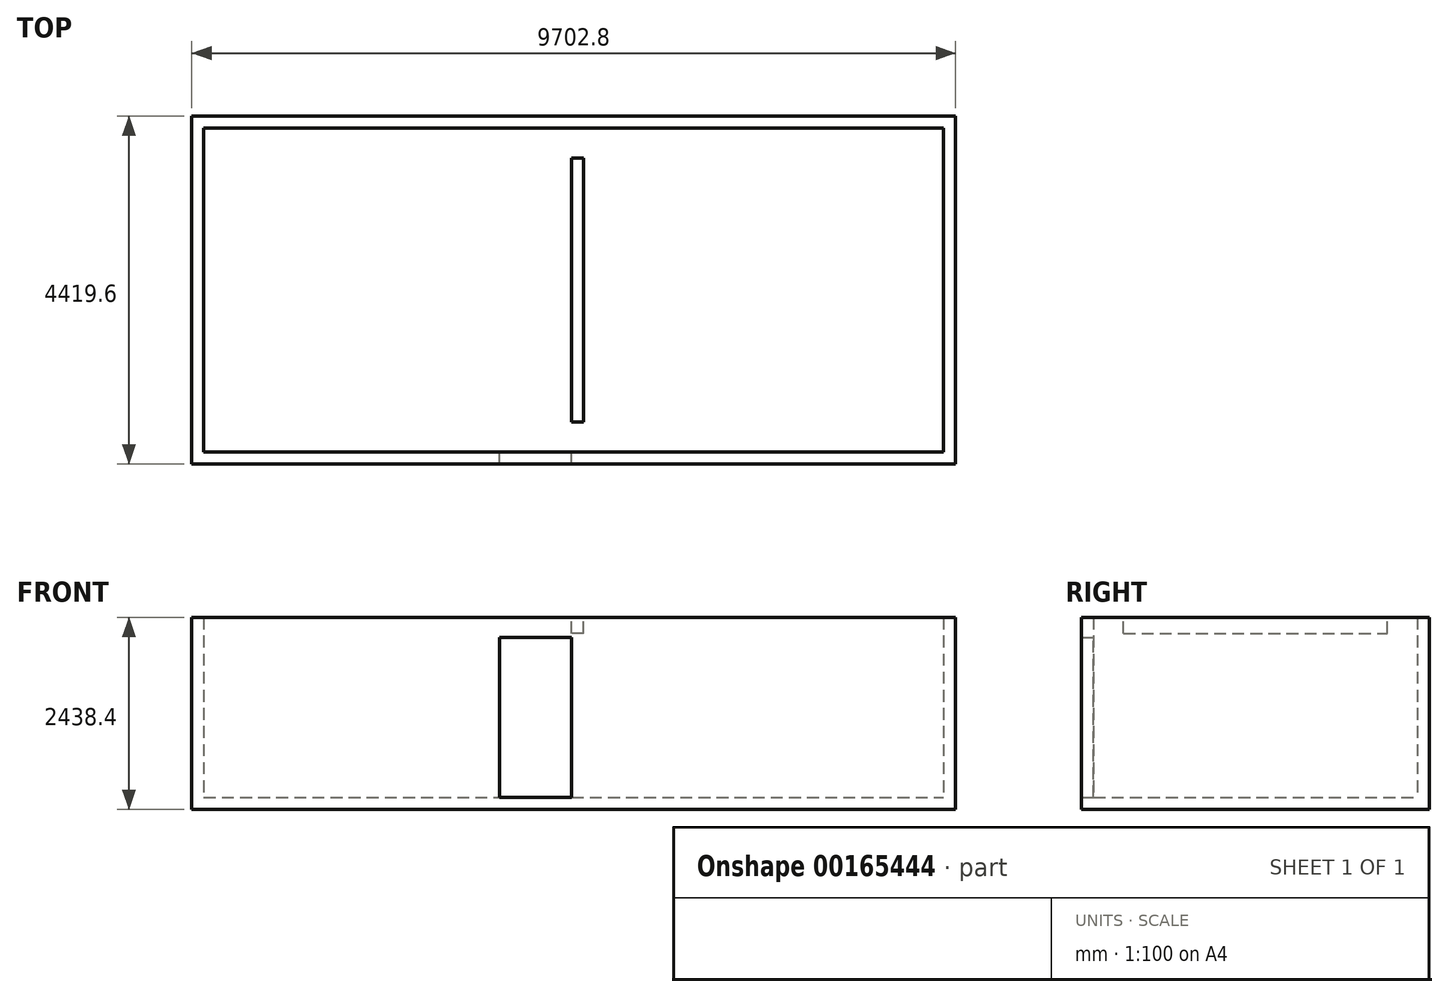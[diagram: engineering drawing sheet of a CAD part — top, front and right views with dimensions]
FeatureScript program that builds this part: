
annotation { "Feature Type Name" : "Feature", "Feature Type Description" : "" }
export const myFeature = defineFeature(function(context is Context, id is Id, definition is map)
    precondition{}
    {
        {
            var Q0;
            Q0=qCreatedBy(makeId("Top.planeOp"),FACE);
            var sketch = newSketch(context, id + "F0", { "sketchPlane" : qUnion([Q0])});
            skLineSegment(sketch, "E0.bottom", {"start": v(0, 0) * mm, "end": v(9398, 0) * mm});
            skLineSegment(sketch, "E0.top", {"start": v(0, 4114.8) * mm, "end": v(9398, 4114.8) * mm});
            skLineSegment(sketch, "E0.left", {"start": v(0, 0) * mm, "end": v(0, 4114.8) * mm});
            skLineSegment(sketch, "E0.right", {"start": v(9398, 0) * mm, "end": v(9398, 4114.8) * mm});
            skLineSegment(sketch, "E1.bottom", {"start": v(4673.6, 4114.8) * mm, "end": v(4826, 4114.8) * mm});
            skLineSegment(sketch, "E1.top", {"start": v(4673.6, 3733.8) * mm, "end": v(4826, 3733.8) * mm});
            skLineSegment(sketch, "E1.left", {"start": v(4673.6, 4114.8) * mm, "end": v(4673.6, 3733.8) * mm});
            skLineSegment(sketch, "E1.right", {"start": v(4826, 4114.8) * mm, "end": v(4826, 3733.8) * mm});
            skLineSegment(sketch, "E2.bottom", {"start": v(4673.6, 0) * mm, "end": v(4826, 0) * mm});
            skLineSegment(sketch, "E2.top", {"start": v(4673.6, 381) * mm, "end": v(4826, 381) * mm});
            skLineSegment(sketch, "E2.left", {"start": v(4673.6, 0) * mm, "end": v(4673.6, 381) * mm});
            skLineSegment(sketch, "E2.right", {"start": v(4826, 0) * mm, "end": v(4826, 381) * mm});
            skLineSegment(sketch, "E3.bottom", {"start": v(-152.4, 4267.2) * mm, "end": v(9550.4, 4267.2) * mm});
            skLineSegment(sketch, "E3.top", {"start": v(-152.4, -152.4) * mm, "end": v(9550.4, -152.4) * mm});
            skLineSegment(sketch, "E3.left", {"start": v(-152.4, 4267.2) * mm, "end": v(-152.4, -152.4) * mm});
            skLineSegment(sketch, "E3.right", {"start": v(9550.4, 4267.2) * mm, "end": v(9550.4, -152.4) * mm});
            skSolve(sketch);
        }
        {
            var Q0;
            {var subQ2=sQuery(id+"F0.wireOp",EDGE,"E0.left");Q0=makeQuery(id+"F0.imprint","IMPRINT",FACE,{"disambiguationData":[TD([[makeQuery(id+"F0.imprint","IMPRINT",EDGE,{"derivedFrom":subQ2}),1.0]])]});}
            var Q1;
            Q1=makeQuery(id+"F0.imprint","IMPRINT",FACE,{"disambiguationData":[TD([[makeQuery(id+"F0.imprint","IMPRINT",EDGE,{"derivedFrom":sQuery(id+"F0.wireOp",EDGE,"E1.bottom")}),-1.0]])]});
            var Q2;
            Q2=makeQuery(id+"F0.imprint","IMPRINT",FACE,{"disambiguationData":[TD([[makeQuery(id+"F0.imprint","IMPRINT",EDGE,{"derivedFrom":sQuery(id+"F0.wireOp",EDGE,"E2.bottom")}),1.0]])]});
            extrude(context, id + "F1", {"entities" : qUnion([Q0, Q1, Q2]), "depth" : 2286 * mm});
        }
        {
            var Q0;
            Q0=makeQuery(id+"F1.opExtrude","CAP_FACE",FACE,{"disambiguationData":[OSD([sQuery(id+"F0.wireOp",EDGE,"E0.bottom"),sQuery(id+"F0.wireOp",EDGE,"E0.top"),sQuery(id+"F0.wireOp",EDGE,"E0.left"),sQuery(id+"F0.wireOp",EDGE,"E0.right"),sQuery(id+"F0.wireOp",EDGE,"E1.top"),sQuery(id+"F0.wireOp",EDGE,"E1.left"),sQuery(id+"F0.wireOp",EDGE,"E1.right"),sQuery(id+"F0.wireOp",EDGE,"E2.top"),sQuery(id+"F0.wireOp",EDGE,"E2.left"),sQuery(id+"F0.wireOp",EDGE,"E2.right"),sQuery(id+"F0.wireOp",EDGE,"E3.bottom"),sQuery(id+"F0.wireOp",EDGE,"E3.top"),sQuery(id+"F0.wireOp",EDGE,"E3.left"),sQuery(id+"F0.wireOp",EDGE,"E3.right")])],"isStart":true});
            var sketch = newSketch(context, id + "F2", { "sketchPlane" : qUnion([Q0])});
            skLineSegment(sketch, "E4.bottom", {"start": v(-152.4, 152.4) * mm, "end": v(9550.4, 152.4) * mm});
            skLineSegment(sketch, "E4.top", {"start": v(-152.4, -4267.2) * mm, "end": v(9550.4, -4267.2) * mm});
            skLineSegment(sketch, "E4.left", {"start": v(-152.4, 152.4) * mm, "end": v(-152.4, -4267.2) * mm});
            skLineSegment(sketch, "E4.right", {"start": v(9550.4, 152.4) * mm, "end": v(9550.4, -4267.2) * mm});
            skSolve(sketch);
        }
        {
            var Q0;
            Q0 = qSketchRegion(id + "F2", true);
            extrude(context, id + "F3", {"entities" : qUnion([Q0]), "operationType" : NewBodyOperationType.ADD, "depth" : 152.4 * mm});
        }
        {
            var Q0;
            {var subQ0=sQuery(id+"F0.wireOp",EDGE,"E0.bottom");Q0=makeQuery(id+"F1.opExtrude","SWEPT_FACE",FACE,{"disambiguationData":[OSD([subQ0]),TDD([makeQuery(id+"F0.imprint","IMPRINT",EDGE,{"disambiguationData":[TD([[makeQuery(id+"F0.imprint","INTERSECT",VERTEX,{"derivedFrom":[subQ0,sQuery(id+"F0.wireOp",EDGE,"E0.left")]}),-1.0]])],"derivedFrom":subQ0})])]});}
            var sketch = newSketch(context, id + "F4", { "sketchPlane" : qUnion([Q0])});
            skLineSegment(sketch, "E5.bottom", {"start": v(-4673.6, 0) * mm, "end": v(-3759.2, 0) * mm});
            skLineSegment(sketch, "E5.top", {"start": v(-4673.6, 2032) * mm, "end": v(-3759.2, 2032) * mm});
            skLineSegment(sketch, "E5.left", {"start": v(-4673.6, 0) * mm, "end": v(-4673.6, 2032) * mm});
            skLineSegment(sketch, "E5.right", {"start": v(-3759.2, 0) * mm, "end": v(-3759.2, 2032) * mm});
            skSolve(sketch);
        }
        {
            var Q0;
            Q0 = qSketchRegion(id + "F4", true);
            extrude(context, id + "F5", {"entities" : qUnion([Q0]), "operationType" : NewBodyOperationType.REMOVE, "endBound" : BoundingType.THROUGH_ALL, "oppositeDirection" : true, "depth" : 25.4 * mm});
        }
        {
            var Q0;
            Q0=makeQuery(id+"F1.opExtrude","CAP_FACE",FACE,{"disambiguationData":[OSD([sQuery(id+"F0.wireOp",EDGE,"E0.bottom"),sQuery(id+"F0.wireOp",EDGE,"E0.top"),sQuery(id+"F0.wireOp",EDGE,"E0.left"),sQuery(id+"F0.wireOp",EDGE,"E0.right"),sQuery(id+"F0.wireOp",EDGE,"E1.top"),sQuery(id+"F0.wireOp",EDGE,"E1.left"),sQuery(id+"F0.wireOp",EDGE,"E1.right"),sQuery(id+"F0.wireOp",EDGE,"E2.top"),sQuery(id+"F0.wireOp",EDGE,"E2.left"),sQuery(id+"F0.wireOp",EDGE,"E2.right"),sQuery(id+"F0.wireOp",EDGE,"E3.bottom"),sQuery(id+"F0.wireOp",EDGE,"E3.top"),sQuery(id+"F0.wireOp",EDGE,"E3.left"),sQuery(id+"F0.wireOp",EDGE,"E3.right")])],"isStart":false});
            var sketch = newSketch(context, id + "F6", { "sketchPlane" : qUnion([Q0])});
            skLineSegment(sketch, "E6.bottom", {"start": v(4826, 381) * mm, "end": v(4673.6, 381) * mm});
            skLineSegment(sketch, "E6.top", {"start": v(4826, 3733.8) * mm, "end": v(4673.6, 3733.8) * mm});
            skLineSegment(sketch, "E6.left", {"start": v(4826, 381) * mm, "end": v(4826, 3733.8) * mm});
            skLineSegment(sketch, "E6.right", {"start": v(4673.6, 381) * mm, "end": v(4673.6, 3733.8) * mm});
            skSolve(sketch);
        }
        {
            var Q0;
            Q0 = qSketchRegion(id + "F6", true);
            extrude(context, id + "F7", {"entities" : qUnion([Q0]), "operationType" : NewBodyOperationType.ADD, "oppositeDirection" : true, "depth" : 203.2 * mm});
        }
    });
